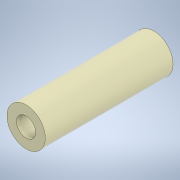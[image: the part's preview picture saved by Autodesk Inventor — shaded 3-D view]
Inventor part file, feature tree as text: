
AUTODESK INVENTOR PART (.ipt)
format: ipt  version: 2020.2 (Build 242310000, 310)  size: 100,864 bytes
history: native  units: mm
features: other x1, extrude x1, sketch x1
ambient origin geometry x8: Origin, YZ Plane, XZ Plane, XY Plane, X Axis, Y Axis, Z Axis, Center Point
bodies: Body1 (feature_tree)
feature tree (3):
  other  "ソリッド1"
  extrude  "押し出し1"  Depth=6.0mm
  sketch  "スケッチ1"
